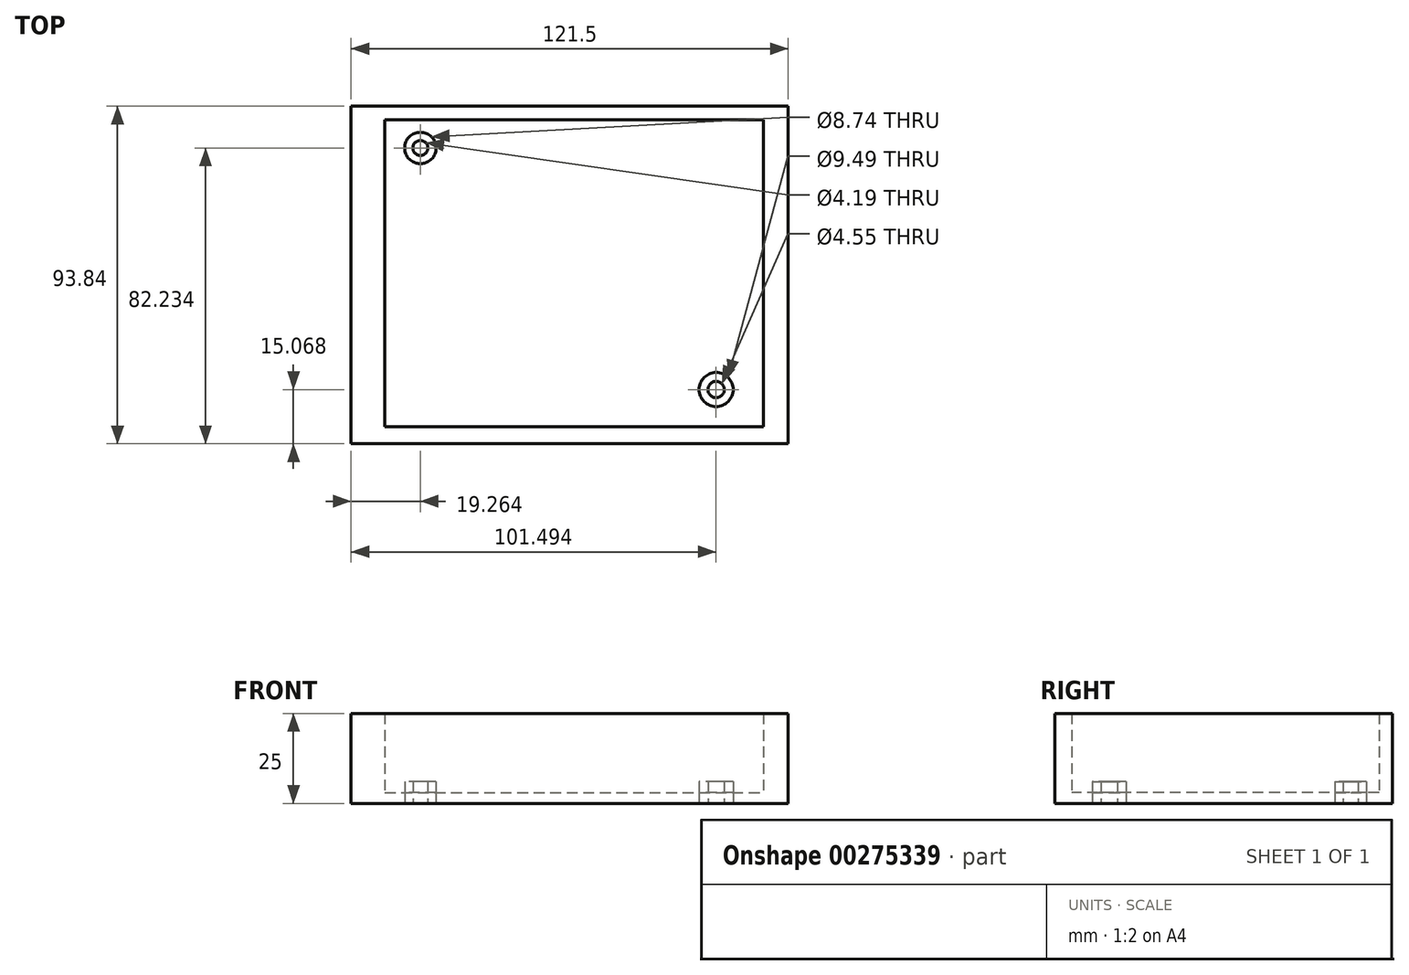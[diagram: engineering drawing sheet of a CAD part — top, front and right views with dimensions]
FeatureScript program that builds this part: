
annotation { "Feature Type Name" : "Feature", "Feature Type Description" : "" }
export const myFeature = defineFeature(function(context is Context, id is Id, definition is map)
    precondition{}
    {
        {
            var Q0;
            Q0=qCreatedBy(makeId("Top.planeOp"),FACE);
            var sketch = newSketch(context, id + "F0", { "sketchPlane" : qUnion([Q0])});
            skLineSegment(sketch, "E0.bottom", {"start": v(-70.38, 37.04) * mm, "end": v(51.12, 37.04) * mm});
            skLineSegment(sketch, "E0.top", {"start": v(-70.38, -56.8) * mm, "end": v(51.12, -56.8) * mm});
            skLineSegment(sketch, "E0.left", {"start": v(-70.38, 37.04) * mm, "end": v(-70.38, -56.8) * mm});
            skLineSegment(sketch, "E0.right", {"start": v(51.12, 37.04) * mm, "end": v(51.12, -56.8) * mm});
            skLineSegment(sketch, "E1.bottom", {"start": v(-61, 33.34) * mm, "end": v(44.2, 33.34) * mm});
            skLineSegment(sketch, "E1.top", {"start": v(-61, -52.1) * mm, "end": v(44.2, -52.1) * mm});
            skLineSegment(sketch, "E1.left", {"start": v(-61, 33.34) * mm, "end": v(-61, -52.1) * mm});
            skLineSegment(sketch, "E1.right", {"start": v(44.2, 33.34) * mm, "end": v(44.2, -52.1) * mm});
            skCircle(sketch, "E2", {"center": v(-51.12, 25.43) * mm, "radius": 4.37 * mm});
            skCircle(sketch, "E3", {"center": v(31.11, -41.73) * mm, "radius": 4.74 * mm});
            skCircle(sketch, "E4", {"center": v(-51.12, 25.43) * mm, "radius": 2.1 * mm});
            skCircle(sketch, "E5", {"center": v(31.11, -41.73) * mm, "radius": 2.28 * mm});
            skSolve(sketch);
        }
        {
            var Q0;
            Q0=makeQuery(id+"F0.imprint","IMPRINT",FACE,{"disambiguationData":[TD([[makeQuery(id+"F0.imprint","IMPRINT",EDGE,{"derivedFrom":sQuery(id+"F0.wireOp",EDGE,"E2")}),1.0]])]});
            var Q1;
            Q1=makeQuery(id+"F0.imprint","IMPRINT",FACE,{"disambiguationData":[TD([[makeQuery(id+"F0.imprint","IMPRINT",EDGE,{"derivedFrom":sQuery(id+"F0.wireOp",EDGE,"E3")}),1.0]])]});
            extrude(context, id + "F1", {"entities" : qUnion([Q0, Q1]), "depth" : 6 * mm});
        }
        {
            var Q0;
            Q0=makeQuery(id+"F0.imprint","IMPRINT",FACE,{"disambiguationData":[TD([[makeQuery(id+"F0.imprint","IMPRINT",EDGE,{"derivedFrom":sQuery(id+"F0.wireOp",EDGE,"E1.bottom")}),-1.0]])]});
            extrude(context, id + "F2", {"entities" : qUnion([Q0]), "depth" : 3 * mm});
        }
        {
            var Q0;
            Q0=makeQuery(id+"F0.imprint","IMPRINT",FACE,{"disambiguationData":[TD([[makeQuery(id+"F0.imprint","IMPRINT",EDGE,{"derivedFrom":sQuery(id+"F0.wireOp",EDGE,"E0.bottom")}),-1.0]])]});
            extrude(context, id + "F3", {"entities" : qUnion([Q0]), "operationType" : NewBodyOperationType.ADD, "depth" : 25 * mm});
        }
    });
